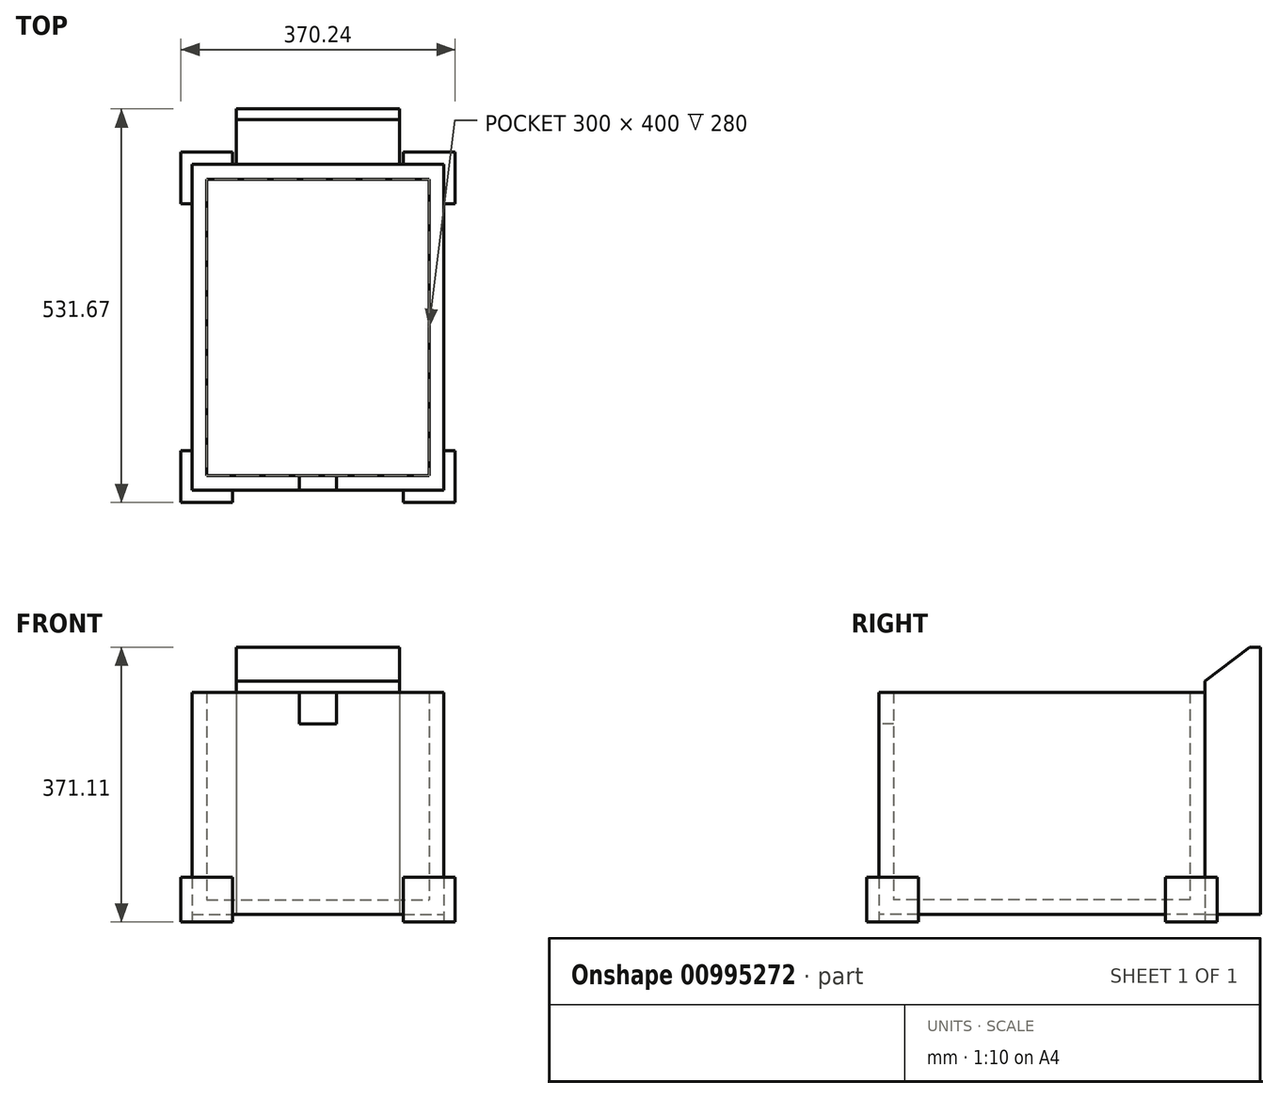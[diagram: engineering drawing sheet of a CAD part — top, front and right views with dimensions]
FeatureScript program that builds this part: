
annotation { "Feature Type Name" : "Feature", "Feature Type Description" : "" }
export const myFeature = defineFeature(function(context is Context, id is Id, definition is map)
    precondition{}
    {
        {
            var Q0;
            Q0=qCreatedBy(makeId("Top.planeOp"),FACE);
            var sketch = newSketch(context, id + "F0", { "sketchPlane" : qUnion([Q0])});
            skLineSegment(sketch, "E0.bottom", {"start": v(-150, 200) * mm, "end": v(150, 200) * mm});
            skLineSegment(sketch, "E0.top", {"start": v(-150, -200) * mm, "end": v(150, -200) * mm});
            skLineSegment(sketch, "E0.left", {"start": v(-150, 200) * mm, "end": v(-150, -200) * mm});
            skLineSegment(sketch, "E0.right", {"start": v(150, 200) * mm, "end": v(150, -200) * mm});
            skLineSegment(sketch, "E1", {"start": v(0, 309.87) * mm, "end": v(0, -271.35) * mm, "construction": true});
            skLineSegment(sketch, "E2", {"start": v(-276.24, 0) * mm, "end": v(279.94, 0) * mm, "construction": true});
            skLineSegment(sketch, "E3.0", {"start": v(170, 220) * mm, "end": v(170, -220) * mm});
            skLineSegment(sketch, "E3.1", {"start": v(-170, 220) * mm, "end": v(170, 220) * mm});
            skLineSegment(sketch, "E3.2", {"start": v(-170, 220) * mm, "end": v(-170, -220) * mm});
            skLineSegment(sketch, "E3.3", {"start": v(-170, -220) * mm, "end": v(170, -220) * mm});
            skLineSegment(sketch, "E4", {"start": v(-110, 220) * mm, "end": v(-110, 295) * mm});
            skLineSegment(sketch, "E5", {"start": v(-110, 295) * mm, "end": v(110, 295) * mm});
            skLineSegment(sketch, "E6", {"start": v(110, 220) * mm, "end": v(110, 295) * mm});
            skLineSegment(sketch, "E7", {"start": v(-170, -166.67) * mm, "end": v(-185.12, -166.67) * mm});
            skLineSegment(sketch, "E8", {"start": v(-185.12, -166.67) * mm, "end": v(-185.12, -236.67) * mm});
            skLineSegment(sketch, "E9", {"start": v(-185.12, -236.67) * mm, "end": v(-115.12, -236.67) * mm});
            skLineSegment(sketch, "E10", {"start": v(-115.12, -236.67) * mm, "end": v(-115.12, -220) * mm});
            skLineSegment(sketch, "E11.MirrorCS", {"start": v(115.12, -236.67) * mm, "end": v(115.12, -220) * mm});
            skLineSegment(sketch, "E12.MirrorCS", {"start": v(185.12, -236.67) * mm, "end": v(115.12, -236.67) * mm});
            skLineSegment(sketch, "E13.MirrorCS", {"start": v(185.12, -166.67) * mm, "end": v(185.12, -236.67) * mm});
            skLineSegment(sketch, "E14.MirrorCS", {"start": v(170, -166.67) * mm, "end": v(185.12, -166.67) * mm});
            skLineSegment(sketch, "E15.MirrorCS", {"start": v(170, 166.67) * mm, "end": v(185.12, 166.67) * mm});
            skLineSegment(sketch, "E16.MirrorCS", {"start": v(185.12, 166.67) * mm, "end": v(185.12, 236.67) * mm});
            skLineSegment(sketch, "E17.MirrorCS", {"start": v(-170, 166.67) * mm, "end": v(-185.12, 166.67) * mm});
            skLineSegment(sketch, "E18.MirrorCS", {"start": v(-185.12, 166.67) * mm, "end": v(-185.12, 236.67) * mm});
            skLineSegment(sketch, "E19.MirrorCS", {"start": v(-185.12, 236.67) * mm, "end": v(-115.12, 236.67) * mm});
            skLineSegment(sketch, "E20.MirrorCS", {"start": v(-115.12, 236.67) * mm, "end": v(-115.12, 220) * mm});
            skLineSegment(sketch, "E21.MirrorCS", {"start": v(185.12, 236.67) * mm, "end": v(115.12, 236.67) * mm});
            skLineSegment(sketch, "E22.MirrorCS", {"start": v(115.12, 236.67) * mm, "end": v(115.12, 220) * mm});
            skSolve(sketch);
        }
        {
            var Q0;
            Q0=makeQuery(id+"F0.imprint","IMPRINT",FACE,{"disambiguationData":[TD([[makeQuery(id+"F0.imprint","IMPRINT",EDGE,{"derivedFrom":sQuery(id+"F0.wireOp",EDGE,"E0.bottom")}),-1.0]])]});
            var Q1;
            Q1=makeQuery(id+"F0.imprint","IMPRINT",FACE,{"disambiguationData":[TD([[makeQuery(id+"F0.imprint","IMPRINT",EDGE,{"derivedFrom":sQuery(id+"F0.wireOp",EDGE,"E0.bottom")}),1.0]])]});
            extrude(context, id + "F1", {"entities" : qUnion([Q0, Q1]), "depth" : 300 * mm, "offsetDistance" : 25 * mm});
        }
        {
            var Q0;
            {var subQ0=sQuery(id+"F0.wireOp",EDGE,"E4");Q0=makeQuery(id+"F0.imprint","IMPRINT",FACE,{"disambiguationData":[TD([[makeQuery(id+"F0.imprint","IMPRINT",EDGE,{"derivedFrom":subQ0}),-1.0]])]});}
            extrude(context, id + "F2", {"entities" : qUnion([Q0]), "operationType" : NewBodyOperationType.ADD, "depth" : 400 * mm, "offsetDistance" : 25 * mm});
        }
        {
            var Q0;
            Q0=makeQuery(id+"F0.imprint","IMPRINT",FACE,{"disambiguationData":[TD([[makeQuery(id+"F0.imprint","IMPRINT",EDGE,{"derivedFrom":sQuery(id+"F0.wireOp",EDGE,"E0.bottom")}),-1.0]])]});
            extrude(context, id + "F3", {"entities" : qUnion([Q0]), "operationType" : NewBodyOperationType.REMOVE, "depth" : 300 * mm, "offsetDistance" : 25 * mm});
        }
        {
            var Q0;
            Q0=makeQuery(id+"F0.imprint","IMPRINT",FACE,{"disambiguationData":[TD([[makeQuery(id+"F0.imprint","IMPRINT",EDGE,{"derivedFrom":sQuery(id+"F0.wireOp",EDGE,"E0.bottom")}),-1.0]])]});
            extrude(context, id + "F4", {"entities" : qUnion([Q0]), "operationType" : NewBodyOperationType.ADD, "depth" : 20 * mm, "offsetDistance" : 25 * mm});
        }
        {
            var Q0;
            Q0=makeQuery(id+"F2.opExtrude","SWEPT_FACE",FACE,{"disambiguationData":[OSD([sQuery(id+"F0.wireOp",EDGE,"E4")])]});
            var sketch = newSketch(context, id + "F5", { "sketchPlane" : qUnion([Q0])});
            skLineSegment(sketch, "E23", {"start": v(-295, 361.1) * mm, "end": v(-280.52, 361.1) * mm});
            skLineSegment(sketch, "E24", {"start": v(-280.52, 361.1) * mm, "end": v(-220, 315.35) * mm});
            skSolve(sketch);
        }
        {
            var Q0;
            {var subQ3=sQuery(id+"F5.wireOp",EDGE,"E23");Q0=makeQuery(id+"F5.imprint","IMPRINT",FACE,{"disambiguationData":[TD([[makeQuery(id+"F5.imprint","IMPRINT",EDGE,{"derivedFrom":subQ3}),1.0]])]});}
            var Q1;
            Q1=makeQuery(id+"F2.opExtrude","SWEPT_FACE",FACE,{"disambiguationData":[OSD([sQuery(id+"F0.wireOp",EDGE,"E6")])]});
            extrude(context, id + "F6", {"entities" : qUnion([Q0]), "operationType" : NewBodyOperationType.REMOVE, "endBound" : BoundingType.UP_TO_SURFACE, "oppositeDirection" : true, "depth" : 25 * mm, "endBoundEntityFace" : qUnion([Q1]), "offsetDistance" : 25 * mm});
        }
        {
            var Q0;
            Q0=makeQuery(id+"F1.opExtrude","SWEPT_FACE",FACE,{"disambiguationData":[OSD([sQuery(id+"F0.wireOp",EDGE,"E3.3")])]});
            var sketch = newSketch(context, id + "F7", { "sketchPlane" : qUnion([Q0])});
            skLineSegment(sketch, "E25", {"start": v(-24.94, 300) * mm, "end": v(-24.94, 257.15) * mm});
            skLineSegment(sketch, "E26", {"start": v(-24.94, 257.15) * mm, "end": v(24.94, 257.15) * mm});
            skLineSegment(sketch, "E27", {"start": v(24.94, 257.15) * mm, "end": v(24.94, 300) * mm});
            skLineSegment(sketch, "E28", {"start": v(0, 300) * mm, "end": v(0, 183.57) * mm, "construction": true});
            skSolve(sketch);
        }
        {
            var Q0;
            {var subQ0=sQuery(id+"F7.wireOp",EDGE,"E25");Q0=makeQuery(id+"F7.imprint","IMPRINT",FACE,{"disambiguationData":[TD([[makeQuery(id+"F7.imprint","IMPRINT",EDGE,{"derivedFrom":subQ0}),1.0]])]});}
            var Q1;
            Q1=makeQuery(id+"F3.boolean.opBoolean","COPY",FACE,{"derivedFrom":makeQuery(id+"F3.opExtrude","SWEPT_FACE",FACE,{"disambiguationData":[OSD([sQuery(id+"F0.wireOp",EDGE,"E0.top")])]})});
            extrude(context, id + "F8", {"entities" : qUnion([Q0]), "operationType" : NewBodyOperationType.REMOVE, "endBound" : BoundingType.UP_TO_SURFACE, "oppositeDirection" : true, "depth" : 25 * mm, "endBoundEntityFace" : qUnion([Q1]), "offsetDistance" : 25 * mm});
        }
        {
            var Q0;
            {var subQ0=sQuery(id+"F0.wireOp",EDGE,"E17.MirrorCS");Q0=makeQuery(id+"F0.imprint","IMPRINT",FACE,{"disambiguationData":[TD([[makeQuery(id+"F0.imprint","IMPRINT",EDGE,{"derivedFrom":subQ0}),-1.0]])]});}
            var Q1;
            {var subQ0=sQuery(id+"F0.wireOp",EDGE,"E7");Q1=makeQuery(id+"F0.imprint","IMPRINT",FACE,{"disambiguationData":[TD([[makeQuery(id+"F0.imprint","IMPRINT",EDGE,{"derivedFrom":subQ0}),1.0]])]});}
            var Q2;
            {var subQ0=sQuery(id+"F0.wireOp",EDGE,"E11.MirrorCS");Q2=makeQuery(id+"F0.imprint","IMPRINT",FACE,{"disambiguationData":[TD([[makeQuery(id+"F0.imprint","IMPRINT",EDGE,{"derivedFrom":subQ0}),-1.0]])]});}
            var Q3;
            {var subQ4=sQuery(id+"F0.wireOp",EDGE,"E15.MirrorCS");Q3=makeQuery(id+"F0.imprint","IMPRINT",FACE,{"disambiguationData":[TD([[makeQuery(id+"F0.imprint","IMPRINT",EDGE,{"derivedFrom":subQ4}),1.0]])]});}
            extrude(context, id + "F9", {"entities" : qUnion([Q0, Q1, Q2, Q3]), "operationType" : NewBodyOperationType.ADD, "depth" : 50 * mm, "offsetDistance" : 25 * mm, "hasSecondDirection" : true, "secondDirectionOppositeDirection" : true, "secondDirectionDepth" : 10 * mm});
        }
    });
